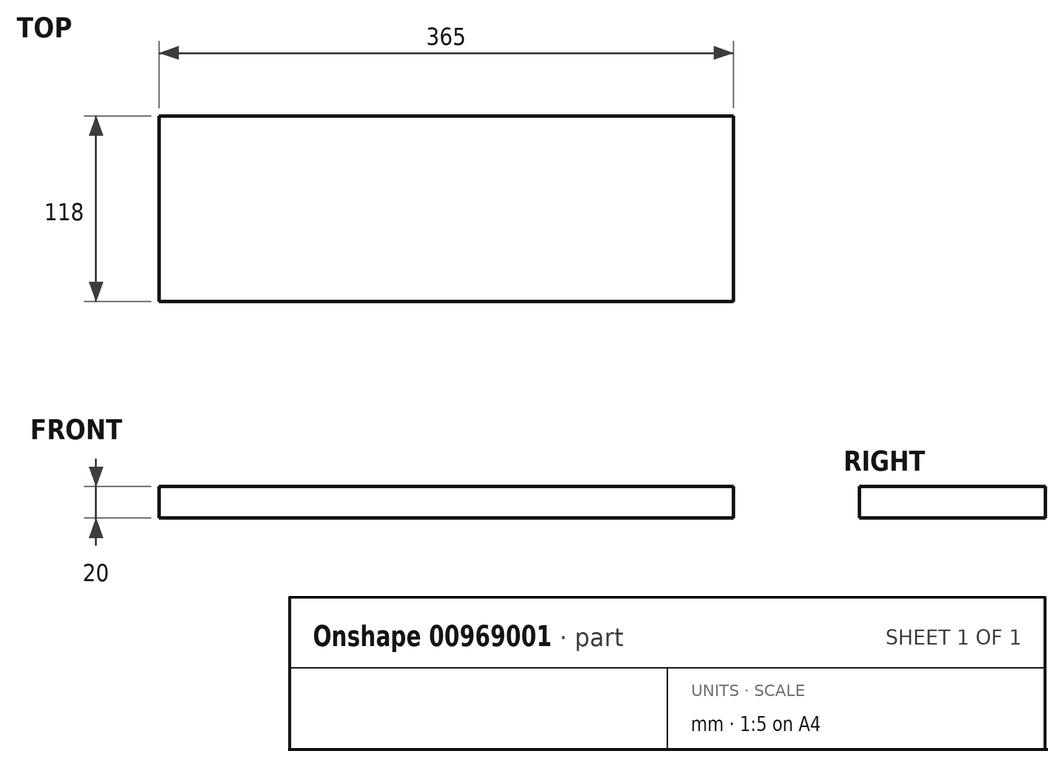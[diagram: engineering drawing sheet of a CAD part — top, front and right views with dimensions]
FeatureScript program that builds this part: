
annotation { "Feature Type Name" : "Feature", "Feature Type Description" : "" }
export const myFeature = defineFeature(function(context is Context, id is Id, definition is map)
    precondition{}
    {
        {
            var Q0;
            Q0=qCreatedBy(makeId("Front.planeOp"),FACE);
            var sketch = newSketch(context, id + "F0", { "sketchPlane" : qUnion([Q0])});
            skLineSegment(sketch, "E0.bottom", {"start": v(182.5, 10) * mm, "end": v(-182.5, 10) * mm});
            skLineSegment(sketch, "E0.top", {"start": v(182.5, -10) * mm, "end": v(-182.5, -10) * mm});
            skLineSegment(sketch, "E0.left", {"start": v(182.5, 10) * mm, "end": v(182.5, -10) * mm});
            skLineSegment(sketch, "E0.right", {"start": v(-182.5, 10) * mm, "end": v(-182.5, -10) * mm});
            skPoint(sketch, "E0.middle", {"position": v(0, 0) * mm});
            skSolve(sketch);
        }
        {
            var Q0;
            Q0=makeQuery(id+"F0.imprint","IMPRINT",FACE,{"disambiguationData":[TD([[makeQuery(id+"F0.imprint","IMPRINT",EDGE,{"derivedFrom":sQuery(id+"F0.wireOp",EDGE,"E0.bottom")}),1.0]])]});
            extrude(context, id + "F1", {"entities" : qUnion([Q0]), "depth" : 118 * mm, "offsetDistance" : 25 * mm});
        }
    });
